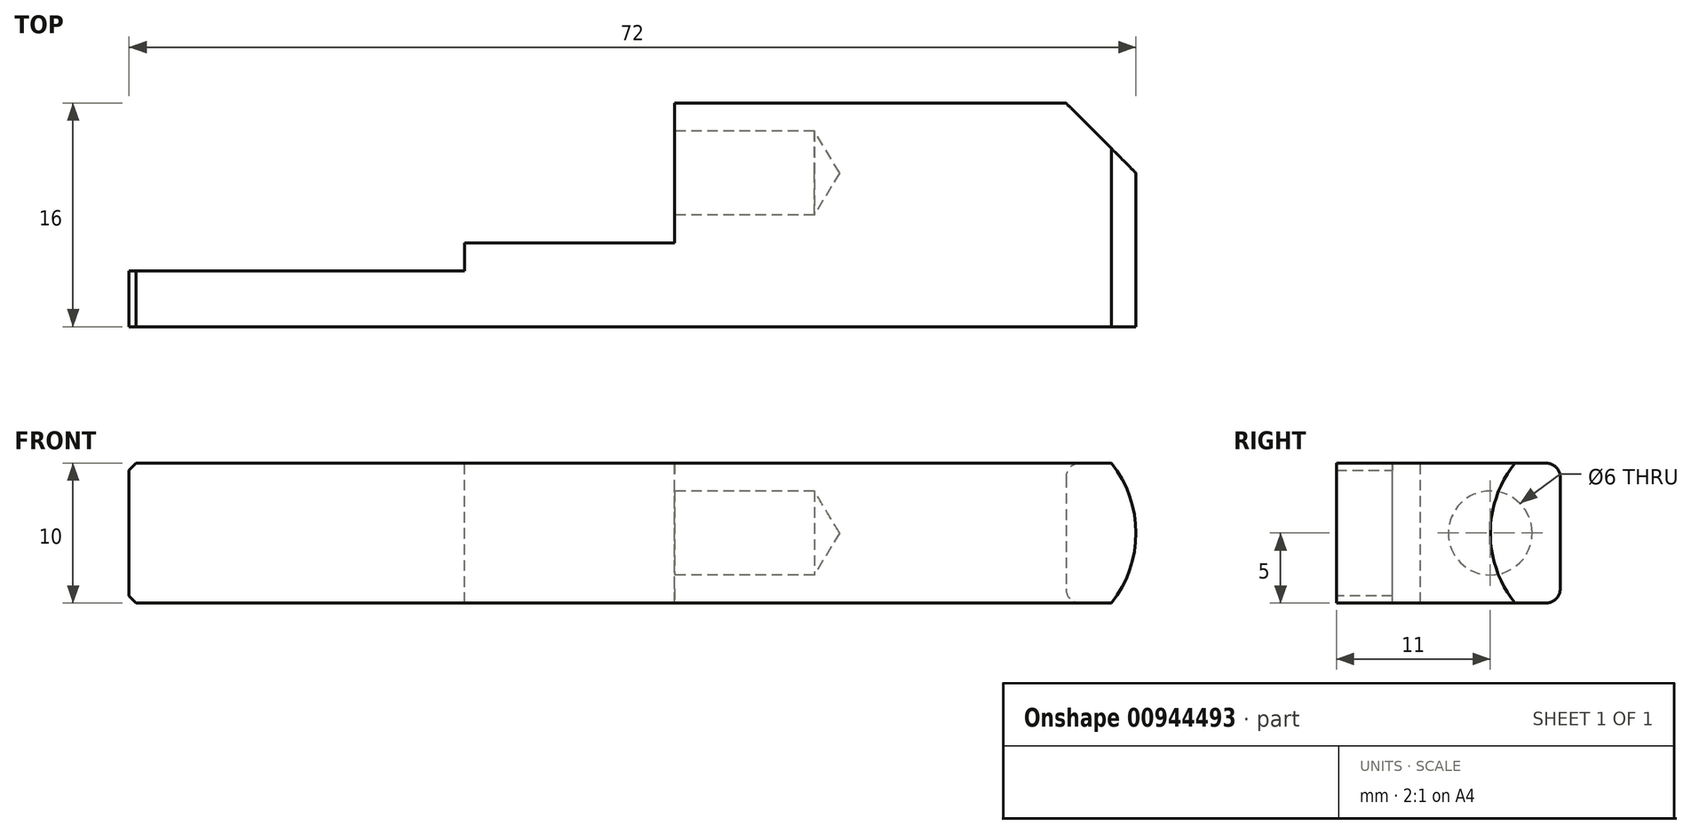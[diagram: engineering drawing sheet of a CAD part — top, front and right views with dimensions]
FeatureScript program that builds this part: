
annotation { "Feature Type Name" : "Feature", "Feature Type Description" : "" }
export const myFeature = defineFeature(function(context is Context, id is Id, definition is map)
    precondition{}
    {
        {
            var Q0;
            Q0=qCreatedBy(makeId("Top.planeOp"),FACE);
            var sketch = newSketch(context, id + "F0", { "sketchPlane" : qUnion([Q0])});
            skLineSegment(sketch, "E0.bottom", {"start": v(36, -8) * mm, "end": v(-36, -8) * mm});
            skLineSegment(sketch, "E0.top", {"start": v(36, 8) * mm, "end": v(-36, 8) * mm});
            skLineSegment(sketch, "E0.left", {"start": v(36, -8) * mm, "end": v(36, 8) * mm});
            skLineSegment(sketch, "E0.right", {"start": v(-36, -8) * mm, "end": v(-36, 8) * mm});
            skPoint(sketch, "E0.middle", {"position": v(0, 0) * mm});
            skSolve(sketch);
        }
        {
            var Q0;
            Q0=makeQuery(id+"F0.imprint","IMPRINT",FACE,{"disambiguationData":[TD([[makeQuery(id+"F0.imprint","IMPRINT",EDGE,{"derivedFrom":sQuery(id+"F0.wireOp",EDGE,"E0.bottom")}),-1.0]])]});
            extrude(context, id + "F1", {"entities" : qUnion([Q0]), "depth" : 10 * mm, "offsetDistance" : 25 * mm});
        }
        {
            var Q0;
            Q0=makeQuery(id+"F1.opExtrude","SWEPT_EDGE",EDGE,{"disambiguationData":[OSD([sQuery(id+"F0.wireOp",EDGE,"E0.top"),sQuery(id+"F0.wireOp",EDGE,"E0.left")])]});
            chamfer(context, id + "F2", {"entities" : qUnion([Q0]), "width" : 5 * mm, "tangentPropagation" : true});
        }
        {
            var Q0;
            Q0=makeQuery(id+"F1.opExtrude","CAP_FACE",FACE,{"disambiguationData":[OSD([sQuery(id+"F0.wireOp",EDGE,"E0.bottom"),sQuery(id+"F0.wireOp",EDGE,"E0.top"),sQuery(id+"F0.wireOp",EDGE,"E0.left"),sQuery(id+"F0.wireOp",EDGE,"E0.right")])],"isStart":false});
            var sketch = newSketch(context, id + "F3", { "sketchPlane" : qUnion([Q0])});
            skLineSegment(sketch, "E1", {"start": v(3, 8) * mm, "end": v(3, -2) * mm});
            skLineSegment(sketch, "E2", {"start": v(3, -2) * mm, "end": v(-12, -2) * mm});
            skLineSegment(sketch, "E3", {"start": v(-12, -2) * mm, "end": v(-12, -4) * mm});
            skLineSegment(sketch, "E4", {"start": v(-12, -4) * mm, "end": v(-36, -4) * mm});
            skLineSegment(sketch, "E5", {"start": v(-36, -4) * mm, "end": v(-36, 8) * mm});
            skLineSegment(sketch, "E6", {"start": v(-36, 8) * mm, "end": v(3, 8) * mm});
            skSolve(sketch);
        }
        {
            var Q0;
            Q0=makeQuery(id+"F3.imprint","IMPRINT",FACE,{"disambiguationData":[TD([[makeQuery(id+"F3.imprint","IMPRINT",EDGE,{"derivedFrom":sQuery(id+"F3.wireOp",EDGE,"E1")}),-1.0]])]});
            extrude(context, id + "F4", {"entities" : qUnion([Q0]), "operationType" : NewBodyOperationType.REMOVE, "endBound" : BoundingType.UP_TO_NEXT, "oppositeDirection" : true, "depth" : 25 * mm, "offsetDistance" : 25 * mm});
        }
        {
            var Q0;
            Q0=makeQuery(id+"F4.boolean.opBoolean","COPY",EDGE,{"derivedFrom":makeQuery(id+"F4.opExtrude","SWEPT_EDGE",EDGE,{"disambiguationData":[OSD([sQuery(id+"F0.wireOp",EDGE,"E0.right"),sQuery(id+"F3.wireOp",EDGE,"E4"),sQuery(id+"F3.wireOp",EDGE,"E5")])]})});
            var Q1;
            Q1=makeQuery(id+"F1.opExtrude","CAP_EDGE",EDGE,{"disambiguationData":[OSD([sQuery(id+"F0.wireOp",EDGE,"E0.right")])],"isStart":false});
            var Q2;
            Q2=makeQuery(id+"F1.opExtrude","CAP_EDGE",EDGE,{"disambiguationData":[OSD([sQuery(id+"F0.wireOp",EDGE,"E0.right")])],"isStart":true});
            chamfer(context, id + "F5", {"entities" : qUnion([Q0, Q1, Q2]), "width" : 0.5 * mm, "tangentPropagation" : true});
        }
        {
            var Q0;
            Q0=makeQuery(id+"F1.opExtrude","CAP_EDGE",EDGE,{"disambiguationData":[OSD([sQuery(id+"F0.wireOp",EDGE,"E0.top")])],"isStart":false});
            var Q1;
            Q1=makeQuery(id+"F1.opExtrude","CAP_EDGE",EDGE,{"disambiguationData":[OSD([sQuery(id+"F0.wireOp",EDGE,"E0.top")])],"isStart":true});
            fillet(context, id + "F6", {"entities" : qUnion([Q0, Q1]), "radius" : 1 * mm, "tangentPropagation" : true, "allowEdgeOverflow" : false});
        }
        {
            var Q0;
            Q0=makeQuery(id+"F1.opExtrude","SWEPT_FACE",FACE,{"disambiguationData":[OSD([sQuery(id+"F0.wireOp",EDGE,"E0.top")])]});
            var sketch = newSketch(context, id + "F7", { "sketchPlane" : qUnion([Q0])});
            skArc(sketch, "E7", {"start": v(-34.24, 10) * mm, "mid": v(-36, 5) * mm, "end": v(-34.24, 0) * mm});
            skPoint(sketch, "E8", {"position": v(-36, 5) * mm});
            skLineSegment(sketch, "E9", {"start": v(-34.24, 10) * mm, "end": v(-36, 10) * mm});
            skLineSegment(sketch, "E10", {"start": v(-36, 10) * mm, "end": v(-36, 0) * mm});
            skLineSegment(sketch, "E11", {"start": v(-36, 0) * mm, "end": v(-34.24, 0) * mm});
            skSolve(sketch);
        }
        {
            var Q0;
            {var subQ0=sQuery(id+"F7.wireOp",EDGE,"E11");Q0=makeQuery(id+"F7.imprint","IMPRINT",FACE,{"disambiguationData":[TD([[makeQuery(id+"F7.imprint","IMPRINT",EDGE,{"derivedFrom":subQ0}),1.0]])]});}
            var Q1;
            {var subQ0=sQuery(id+"F7.wireOp",EDGE,"E9");Q1=makeQuery(id+"F7.imprint","IMPRINT",FACE,{"disambiguationData":[TD([[makeQuery(id+"F7.imprint","IMPRINT",EDGE,{"derivedFrom":subQ0}),1.0]])]});}
            extrude(context, id + "F8", {"entities" : qUnion([Q0, Q1]), "operationType" : NewBodyOperationType.REMOVE, "oppositeDirection" : true, "depth" : 25 * mm, "offsetDistance" : 25 * mm});
        }
        {
            var Q0;
            Q0=makeQuery(id+"F4.boolean.opBoolean","COPY",FACE,{"derivedFrom":makeQuery(id+"F4.opExtrude","SWEPT_FACE",FACE,{"disambiguationData":[OSD([sQuery(id+"F3.wireOp",EDGE,"E1")])]})});
            var sketch = newSketch(context, id + "F9", { "sketchPlane" : qUnion([Q0])});
            skLineSegment(sketch, "E12", {"start": v(-11.06, 5) * mm, "end": v(11.98, 5) * mm, "construction": true});
            skPoint(sketch, "E13", {"position": v(-3, 5) * mm});
            skSolve(sketch);
        }
        {
            var Q0;
            Q0=sQuery(id+"F9.wireOp",VERTEX,"E13");
            var Q1;
            Q1=makeQuery(id+"F1.opExtrude","SWEPT_BODY",BODY,{"disambiguationData":[OSD([sQuery(id+"F0.wireOp",EDGE,"E0.bottom"),sQuery(id+"F0.wireOp",EDGE,"E0.top"),sQuery(id+"F0.wireOp",EDGE,"E0.left"),sQuery(id+"F0.wireOp",EDGE,"E0.right")])]});
            hole(context, id + "F10", {"style" : HoleStyle.SIMPLE, "endStyle" : HoleEndStyle.BLIND, "holeDiameter" : 6 * mm, "majorDiameter" : 5 * mm, "holeDepth" : 10 * mm, "isTappedThrough" : true, "tappedDepth" : 8.5 * mm, "tapClearance" : 3, "startFromSketch" : true, "locations" : qUnion([Q0]), "scope" : qUnion([Q1])});
        }
    });
